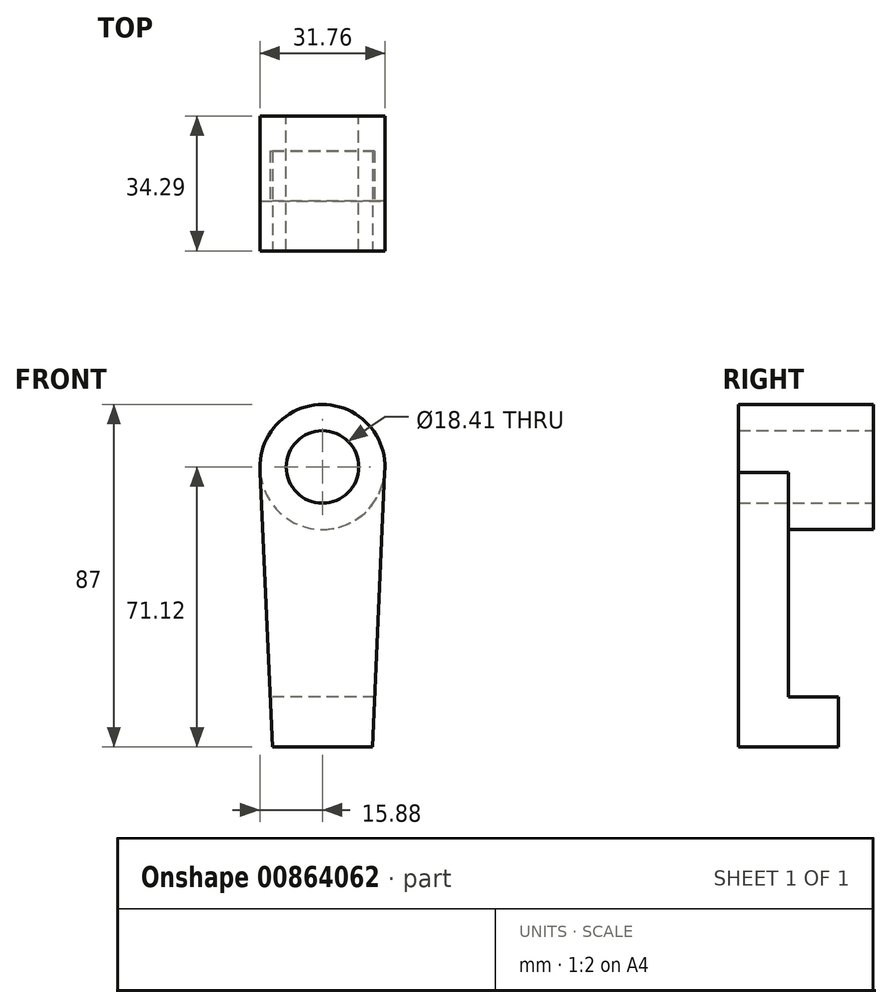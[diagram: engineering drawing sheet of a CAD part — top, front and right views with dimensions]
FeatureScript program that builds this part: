
annotation { "Feature Type Name" : "Feature", "Feature Type Description" : "" }
export const myFeature = defineFeature(function(context is Context, id is Id, definition is map)
    precondition{}
    {
        {
            var Q0;
            Q0=qCreatedBy(makeId("Front.planeOp"),FACE);
            var sketch = newSketch(context, id + "F0", { "sketchPlane" : qUnion([Q0])});
            skCircle(sketch, "E0", {"center": v(0, 0) * mm, "radius": 9.2 * mm});
            skCircle(sketch, "E1", {"center": v(0, 0) * mm, "radius": 15.88 * mm});
            skSolve(sketch);
        }
        {
            var Q0;
            Q0 = qSketchRegion(id + "F0", true);
            extrude(context, id + "F1", {"entities" : qUnion([Q0]), "depth" : 34.3 * mm, "offsetDistance" : 25.4 * mm});
        }
        {
            var Q0;
            Q0=makeQuery(id+"F1.opExtrude","CAP_FACE",FACE,{"disambiguationData":[OSD([sQuery(id+"F0.wireOp",EDGE,"E0"),sQuery(id+"F0.wireOp",EDGE,"E1")])],"isStart":false});
            var sketch = newSketch(context, id + "F2", { "sketchPlane" : qUnion([Q0])});
            skLineSegment(sketch, "E2", {"start": v(15.88, 0) * mm, "end": v(12.7, -71.12) * mm});
            skLineSegment(sketch, "E3", {"start": v(0, 0) * mm, "end": v(0, -71.12) * mm, "construction": true});
            skLineSegment(sketch, "E4", {"start": v(0, -71.12) * mm, "end": v(12.7, -71.12) * mm, "construction": true});
            skLineSegment(sketch, "E5", {"start": v(0, -71.12) * mm, "end": v(-12.7, -71.12) * mm, "construction": true});
            skLineSegment(sketch, "E6", {"start": v(-15.88, 0) * mm, "end": v(-12.7, -71.12) * mm});
            skArc(sketch, "E7.0", {"start": v(-15.88, 0) * mm, "mid": v(0, -15.88) * mm, "end": v(15.88, 0) * mm});
            skLineSegment(sketch, "E8", {"start": v(-12.7, -71.12) * mm, "end": v(12.7, -71.12) * mm});
            skSolve(sketch);
        }
        {
            var Q0;
            Q0 = qSketchRegion(id + "F2", true);
            extrude(context, id + "F3", {"entities" : qUnion([Q0]), "operationType" : NewBodyOperationType.ADD, "oppositeDirection" : true, "depth" : 12.7 * mm, "offsetDistance" : 25.4 * mm});
        }
        {
            var Q0;
            Q0=makeQuery(id+"F3.opExtrude","CAP_FACE",FACE,{"disambiguationData":[OSD([sQuery(id+"F2.wireOp",EDGE,"E2"),sQuery(id+"F2.wireOp",EDGE,"E6"),sQuery(id+"F2.wireOp",EDGE,"E7.0"),sQuery(id+"F2.wireOp",EDGE,"E8")])],"isStart":false});
            var sketch = newSketch(context, id + "F4", { "sketchPlane" : qUnion([Q0])});
            skLineSegment(sketch, "E9", {"start": v(-12.7, -71.12) * mm, "end": v(12.7, -71.12) * mm});
            skLineSegment(sketch, "E10", {"start": v(12.7, -71.12) * mm, "end": v(12.7, -71.12) * mm});
            skLineSegment(sketch, "E11", {"start": v(-12.7, -71.12) * mm, "end": v(-12.7, -71.12) * mm});
            skLineSegment(sketch, "E12", {"start": v(12.7, -71.12) * mm, "end": v(13.27, -58.42) * mm});
            skLineSegment(sketch, "E13", {"start": v(-12.7, -71.12) * mm, "end": v(-13.27, -58.42) * mm});
            skLineSegment(sketch, "E14", {"start": v(-13.27, -58.42) * mm, "end": v(13.27, -58.42) * mm});
            skSolve(sketch);
        }
        {
            var Q0;
            Q0 = qSketchRegion(id + "F4", true);
            extrude(context, id + "F5", {"entities" : qUnion([Q0]), "operationType" : NewBodyOperationType.ADD, "depth" : 12.7 * mm, "offsetDistance" : 25.4 * mm});
        }
    });
